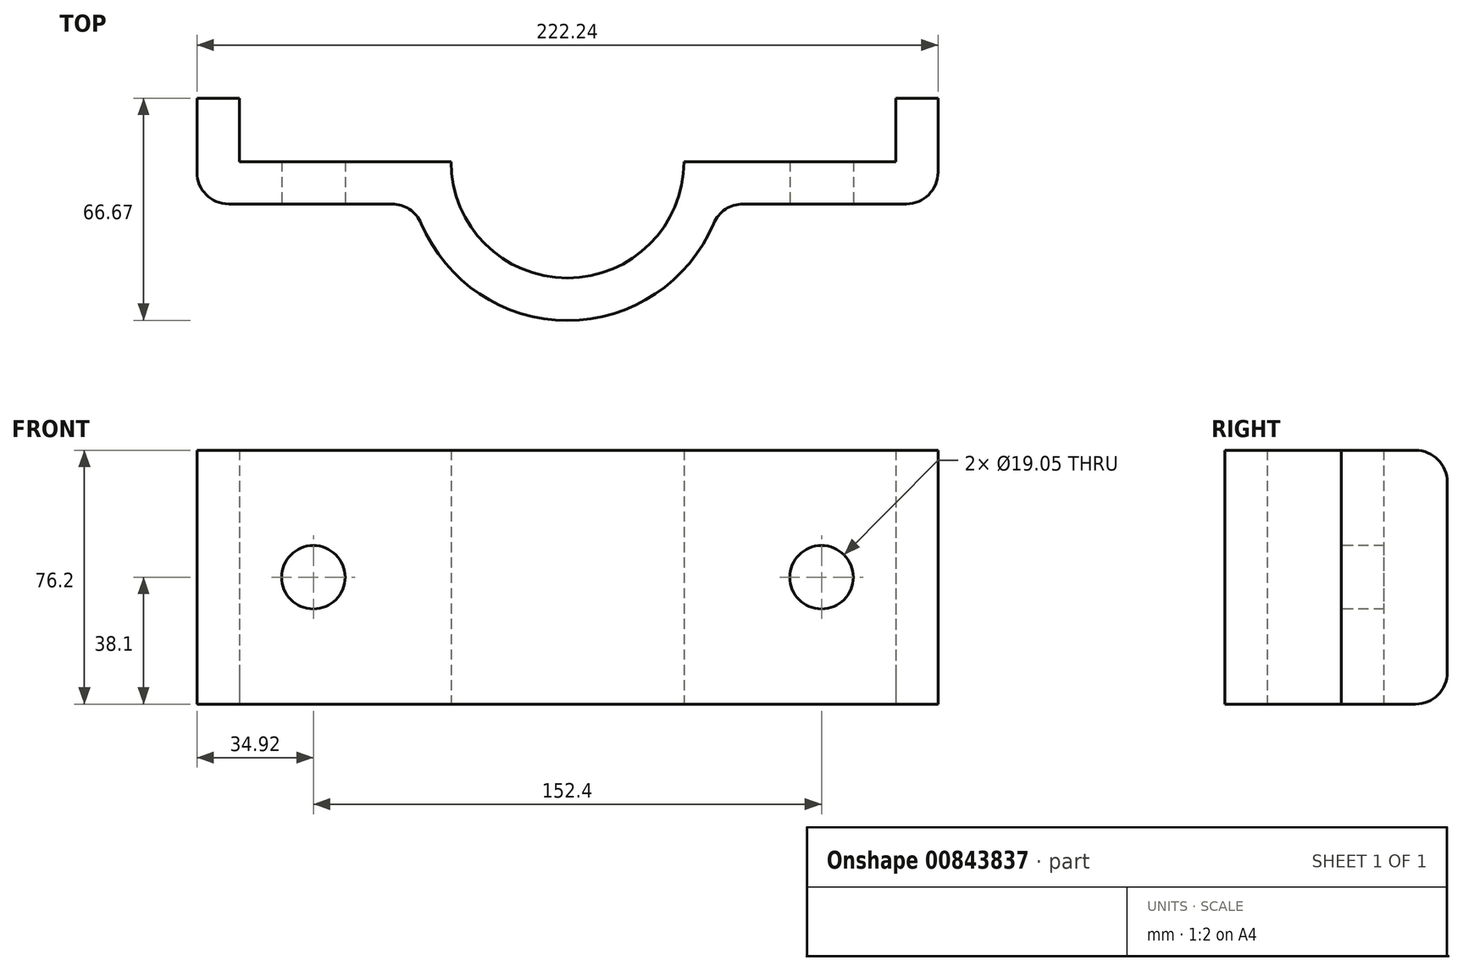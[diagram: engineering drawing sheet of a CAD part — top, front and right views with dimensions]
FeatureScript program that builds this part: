
annotation { "Feature Type Name" : "Feature", "Feature Type Description" : "" }
export const myFeature = defineFeature(function(context is Context, id is Id, definition is map)
    precondition{}
    {
        {
            var Q0;
            Q0=qCreatedBy(makeId("Top.planeOp"),FACE);
            var sketch = newSketch(context, id + "F0", { "sketchPlane" : qUnion([Q0])});
            skArc(sketch, "E0", {"start": v(-43.88, -18.52) * mm, "mid": v(0, -47.63) * mm, "end": v(43.88, -18.52) * mm});
            skArc(sketch, "E1", {"start": v(-34.93, 0) * mm, "mid": v(0, -34.93) * mm, "end": v(34.93, 0) * mm});
            skLineSegment(sketch, "E2", {"start": v(47.63, 0) * mm, "end": v(98.43, 0) * mm});
            skLineSegment(sketch, "E3", {"start": v(111.13, 0) * mm, "end": v(111.13, -3.17) * mm});
            skLineSegment(sketch, "E4", {"start": v(52.65, -12.7) * mm, "end": v(101.6, -12.7) * mm});
            skLineSegment(sketch, "E5", {"start": v(-47.63, 0) * mm, "end": v(-98.43, 0) * mm});
            skLineSegment(sketch, "E6", {"start": v(-111.12, 0) * mm, "end": v(-111.12, -3.18) * mm});
            skLineSegment(sketch, "E7", {"start": v(-101.6, -12.7) * mm, "end": v(-52.65, -12.7) * mm});
            skLineSegment(sketch, "E8", {"start": v(-47.63, 0) * mm, "end": v(-34.93, 0) * mm});
            skLineSegment(sketch, "E9.trimOffspring", {"start": v(34.93, 0) * mm, "end": v(47.63, 0) * mm});
            skArc(sketch, "E10.filletArc", {"start": v(-43.88, -18.52) * mm, "mid": v(-47.39, -14.29) * mm, "end": v(-52.65, -12.7) * mm});
            skPoint(sketch, "E11.newPointB", {"position": v(45.23, -12.7) * mm});
            skArc(sketch, "E11.filletArc", {"start": v(52.65, -12.7) * mm, "mid": v(47.39, -14.29) * mm, "end": v(43.88, -18.52) * mm});
            skLineSegment(sketch, "E12.top", {"start": v(-111.13, 19.05) * mm, "end": v(-98.43, 19.05) * mm});
            skLineSegment(sketch, "E12.left", {"start": v(-111.13, 0) * mm, "end": v(-111.13, 19.05) * mm});
            skLineSegment(sketch, "E12.right", {"start": v(-98.43, 0) * mm, "end": v(-98.43, 19.05) * mm});
            skLineSegment(sketch, "E13.top", {"start": v(111.13, 19.05) * mm, "end": v(98.43, 19.05) * mm});
            skLineSegment(sketch, "E13.left", {"start": v(111.13, 0) * mm, "end": v(111.13, 19.05) * mm});
            skLineSegment(sketch, "E13.right", {"start": v(98.43, 0) * mm, "end": v(98.43, 19.05) * mm});
            skPoint(sketch, "E14.visualSharp", {"position": v(111.13, -12.7) * mm});
            skArc(sketch, "E14.filletArc", {"start": v(101.6, -12.7) * mm, "mid": v(108.34, -9.91) * mm, "end": v(111.13, -3.17) * mm});
            skPoint(sketch, "E15.visualSharp", {"position": v(-111.12, -12.7) * mm});
            skArc(sketch, "E15.filletArc", {"start": v(-111.13, -3.18) * mm, "mid": v(-108.34, -9.91) * mm, "end": v(-101.6, -12.7) * mm});
            skSolve(sketch);
        }
        {
            var Q0;
            Q0=makeQuery(id+"F0.imprint","IMPRINT",FACE,{"disambiguationData":[TD([[makeQuery(id+"F0.imprint","IMPRINT",EDGE,{"derivedFrom":sQuery(id+"F0.wireOp",EDGE,"E0")}),1.0]])]});
            extrude(context, id + "F1", {"entities" : qUnion([Q0]), "depth" : 76.2 * mm, "offsetDistance" : 25.4 * mm});
        }
        {
            var Q0;
            Q0=makeQuery(id+"F1.opExtrude","SWEPT_FACE",FACE,{"disambiguationData":[OSD([sQuery(id+"F0.wireOp",EDGE,"E7")])]});
            var sketch = newSketch(context, id + "F2", { "sketchPlane" : qUnion([Q0])});
            skCircle(sketch, "E16", {"center": v(-76.2, 38.1) * mm, "radius": 9.53 * mm});
            skCircle(sketch, "E17", {"center": v(76.2, 38.1) * mm, "radius": 9.53 * mm});
            skSolve(sketch);
        }
        {
            var Q0;
            Q0 = qSketchRegion(id + "F2", true);
            extrude(context, id + "F3", {"entities" : qUnion([Q0]), "operationType" : NewBodyOperationType.REMOVE, "oppositeDirection" : true, "depth" : 25.4 * mm, "offsetDistance" : 25.4 * mm});
        }
        {
            var Q0;
            Q0=makeQuery(id+"F1.opExtrude","CAP_EDGE",EDGE,{"disambiguationData":[OSD([sQuery(id+"F0.wireOp",EDGE,"E13.top")])],"isStart":false});
            fillet(context, id + "F4", {"entities" : qUnion([Q0]), "radius" : 9.52 * mm, "tangentPropagation" : true, "allowEdgeOverflow" : false});
        }
        {
            var Q0;
            Q0=makeQuery(id+"F1.opExtrude","CAP_EDGE",EDGE,{"disambiguationData":[OSD([sQuery(id+"F0.wireOp",EDGE,"E12.top")])],"isStart":false});
            fillet(context, id + "F5", {"entities" : qUnion([Q0]), "radius" : 9.52 * mm, "tangentPropagation" : true, "allowEdgeOverflow" : false});
        }
        {
            var Q0;
            Q0=makeQuery(id+"F1.opExtrude","CAP_EDGE",EDGE,{"disambiguationData":[OSD([sQuery(id+"F0.wireOp",EDGE,"E13.top")])],"isStart":true});
            var Q1;
            Q1=makeQuery(id+"F1.opExtrude","CAP_EDGE",EDGE,{"disambiguationData":[OSD([sQuery(id+"F0.wireOp",EDGE,"E12.top")])],"isStart":true});
            fillet(context, id + "F6", {"entities" : qUnion([Q0, Q1]), "radius" : 9.52 * mm, "tangentPropagation" : true, "allowEdgeOverflow" : false});
        }
    });
